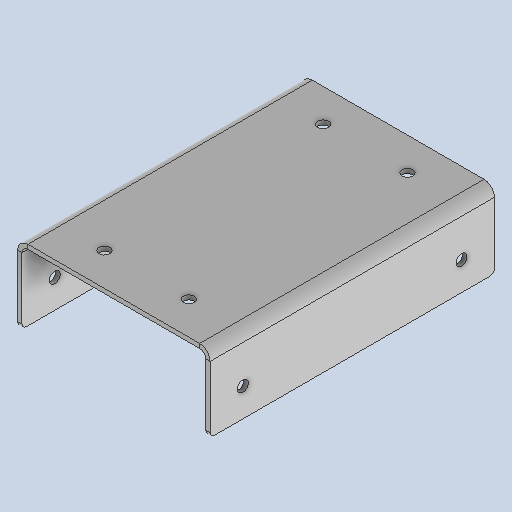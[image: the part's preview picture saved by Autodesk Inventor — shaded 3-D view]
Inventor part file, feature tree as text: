
AUTODESK INVENTOR PART (.ipt)
format: ipt  version: 2025 (Build 290162010, 162A)  size: 236,032 bytes
history: native  units: mm
features: sheet_metal_op x4, sketch x4, other x3, extrude x2, fillet x1, pattern_linear x1
ambient origin geometry x8: Origin, YZ Plane, XZ Plane, XY Plane, X Axis, Y Axis, Z Axis, Center Point
bodies: Solid1 (feature_tree)
feature tree (15):
  sheet_metal_op  "Face1"
  sheet_metal_op  "Flange1"
  extrude  "Extrusion1"  Depth=130.0mm
  extrude  "Extrusion3"  Depth=2.0mm
  fillet  "Fillet1"  Radius=1.0mm
  pattern_linear  "Rectangular Pattern2"  Spacing1=35.0mm  [1 undecoded]
  sketch  "Sketch1"  dims[d0=84.0mm d1=130.0mm]
  other  "Plate1"
  sketch  "Sketch2"  dims[d2=2.0mm d3=2.0mm d4=1.0mm]
  other  "Plate2"
  sheet_metal_op  "Bend1"
  sheet_metal_op  "Corner1"
  sketch  "Sketch3"  dims[d5=4.0mm]
  sketch  "Sketch6"  dims[d6=2.75mm d7=35.0mm d8=90.0deg d9=2.75mm d10=8.0mm d11=2.0mm d12=2.75mm d14=0.0mm d15=13.0mm d17=2.5mm d18=15.0mm d19=0.0mm d20=0.0mm d26=2.0mm d27=5.0mm d28=10.0mm d29=0.0mm d30=20.0mm d32=100.0mm d33=20.0mm]
  other  "Definition1"
note: 1 required parameter value undecoded (feature->parameter linkage not recoverable at this tier; creation-order binding heuristic only, values carry confidence <= 0.55)
